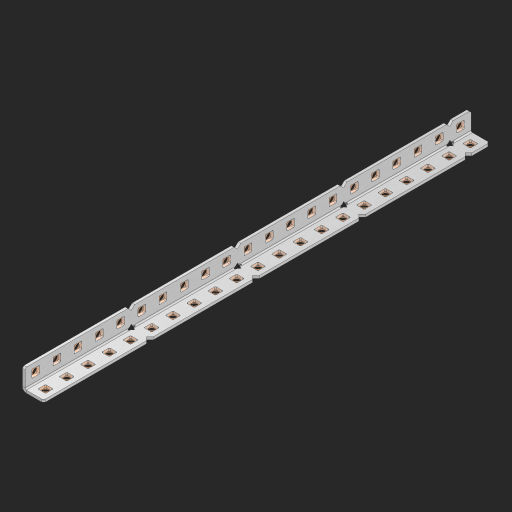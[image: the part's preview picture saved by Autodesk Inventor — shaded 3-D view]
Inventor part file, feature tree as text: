
AUTODESK INVENTOR PART (.ipt)
format: ipt  version: 2023 (Build 270158000, 158)  size: 839,168 bytes
history: native  units: in
note: dims shown in document units (in); Inventor stores cm internally (conversion verified against a paired STEP export)
features: other x48, extrude x43, sheet_metal_op x8, sketch x5, pattern_linear x1, mirror x1, chamfer x1
ambient origin geometry x8: Origin, YZ Plane, XZ Plane, XY Plane, X Axis, Y Axis, Z Axis, Center Point
bodies: Solid1 (feature_tree), Body (feature_tree)
feature tree (107):
  sheet_metal_op  "Flanges"
  sheet_metal_op  "Body Pattern"
  other  "Arc Length"
  pattern_linear  "Notch Pattern"  Spacing1=0.125in  [1 undecoded]
  other  "Diagonal Plane"
  mirror  "Everything Mirrored"
  chamfer  "End Chamfer"
  sketch  "Sketch1"  dims[d0=0.5in]
  other  "Plate1"
  sketch  "Sketch2"  dims[d1=10.5in]
  other  "Plate2"
  sheet_metal_op  "Bend1"
  sheet_metal_op  "Corner1"
  sketch  "Sketch8"  dims[d2=0.0625in]
  sketch  "Sketch9"  dims[d3=0.0625in]
  other  "Srf91"
  sheet_metal_op  "Body Pattern Sketch"
  other  "Srf92"
  sketch  "Sketch13"  dims[d4=0.0312in d5=0.125in d6=0.0625in d7=0.5in d8=90.0deg d9=0.0312in d10=0.25in d11=0.0625in d12=0.0625in d49=0.182in d50=0.02in d52=0.25in d53=0.0625in d54=0.0in d55=0.172in d56=1.0in d57=0.0in d85=0.1473in d86=0.1782in d89=0.0625in d90=0.0in d91=0.04in d92=0.0491in d95=2.5in d96=0.04in d97=0.25in d98=45.0deg d123=0.204in d126=0.0491in d127=0.1473in d128=0.08in d129=0.04in d130=2.5in d131=8.2677in d133=0.5in d134=0.3937in d136=1.0in]
  other  "Srf856"
  other  "Srf857"
  other  "Srf858"
  other  "Srf859"
  other  "Srf860"
  other  "Srf861"
  other  "Srf1275"
  other  "Srf1276"
  other  "Srf1278"
  other  "Srf1279"
  other  "Srf1280"
  other  "Srf1281"
  other  "Srf1282"
  other  "Srf1283"
  other  "Srf1383"
  other  "Srf1384"
  other  "Srf1385"
  other  "Srf1386"
  other  "Srf1387"
  other  "Srf1388"
  other  "Srf1389"
  other  "Srf1390"
  other  "Srf1391"
  other  "Srf1392"
  other  "Srf1393"
  other  "Srf1394"
  other  "Srf1395"
  other  "Srf1396"
  other  "Srf1475"
  other  "Srf1476"
  other  "Srf1477"
  other  "Srf1478"
  other  "Srf1479"
  other  "Srf1480"
  other  "Srf1481"
  other  "Srf1482"
  other  "Srf1483"
  other  "Srf1484"
  other  "Srf1485"
  other  "Srf1486"
  other  "Srf1487"
  other  "Srf1488"
  sheet_metal_op  "Body Stamp"
  sheet_metal_op  "Body Circle"
  sheet_metal_op  "Notch"
  extrude  "ExtrusionSrf92"  Depth=0.0625in
  extrude  "ExtrusionSrf856"  Depth=0.5in TaperAngle=90.0deg
  extrude  "ExtrusionSrf857"  Depth=0.25in
  extrude  "ExtrusionSrf858"  Depth=0.0625in
  extrude  "ExtrusionSrf859"  Depth=0.0625in
  extrude  "ExtrusionSrf860"  Depth=0.3937in
  extrude  "ExtrusionSrf861"  Depth=0.02in
  extrude  "ExtrusionSrf1275"  Depth=0.25in
  extrude  "ExtrusionSrf1276"  Depth=0.0625in
  extrude  "ExtrusionSrf1277"  TaperAngle=0.0deg  [1 undecoded]
  extrude  "ExtrusionSrf1278"  Depth=0.3937in
  extrude  "ExtrusionSrf1279"  Depth=0.3937in TaperAngle=0.0deg
  extrude  "ExtrusionSrf1280"  Depth=0.3937in
  extrude  "ExtrusionSrf1281"  Depth=0.3937in
  extrude  "ExtrusionSrf1282"  Depth=0.0625in
  extrude  "ExtrusionSrf1383"  Depth=0.3937in TaperAngle=0.0deg
  extrude  "ExtrusionSrf1384"  Depth=0.3937in
  extrude  "ExtrusionSrf1385"  Depth=0.25in TaperAngle=45.0deg
  extrude  "ExtrusionSrf1386"  Depth=0.3937in
  extrude  "ExtrusionSrf1387"  Depth=0.3937in
  extrude  "ExtrusionSrf1388"  Depth=0.3937in
  extrude  "ExtrusionSrf1389"  Depth=0.3937in
  extrude  "ExtrusionSrf1390"  Depth=0.3937in
  extrude  "ExtrusionSrf1391"  Depth=0.3937in
  extrude  "ExtrusionSrf1392"  Depth=0.3937in
  extrude  "ExtrusionSrf1393"  Depth=0.5in
  extrude  "ExtrusionSrf1394"  [1 undecoded]
  extrude  "ExtrusionSrf1395"  [1 undecoded]
  extrude  "ExtrusionSrf1396"  [1 undecoded]
  extrude  "ExtrusionSrf1475"  [1 undecoded]
  extrude  "ExtrusionSrf1476"  [1 undecoded]
  extrude  "ExtrusionSrf1477"  [1 undecoded]
  extrude  "ExtrusionSrf1478"  [1 undecoded]
  extrude  "ExtrusionSrf1479"  [1 undecoded]
  extrude  "ExtrusionSrf1480"  [1 undecoded]
  extrude  "ExtrusionSrf1481"  [1 undecoded]
  extrude  "ExtrusionSrf1482"  [1 undecoded]
  extrude  "ExtrusionSrf1483"  [1 undecoded]
  extrude  "ExtrusionSrf1484"  [1 undecoded]
  extrude  "ExtrusionSrf1485"  [1 undecoded]
  extrude  "ExtrusionSrf1486"  [1 undecoded]
  extrude  "ExtrusionSrf1487"  [1 undecoded]
  extrude  "ExtrusionSrf1488"  [1 undecoded]
note: 19 required parameter values undecoded (feature->parameter linkage not recoverable at this tier; creation-order binding heuristic only, values carry confidence <= 0.55)
